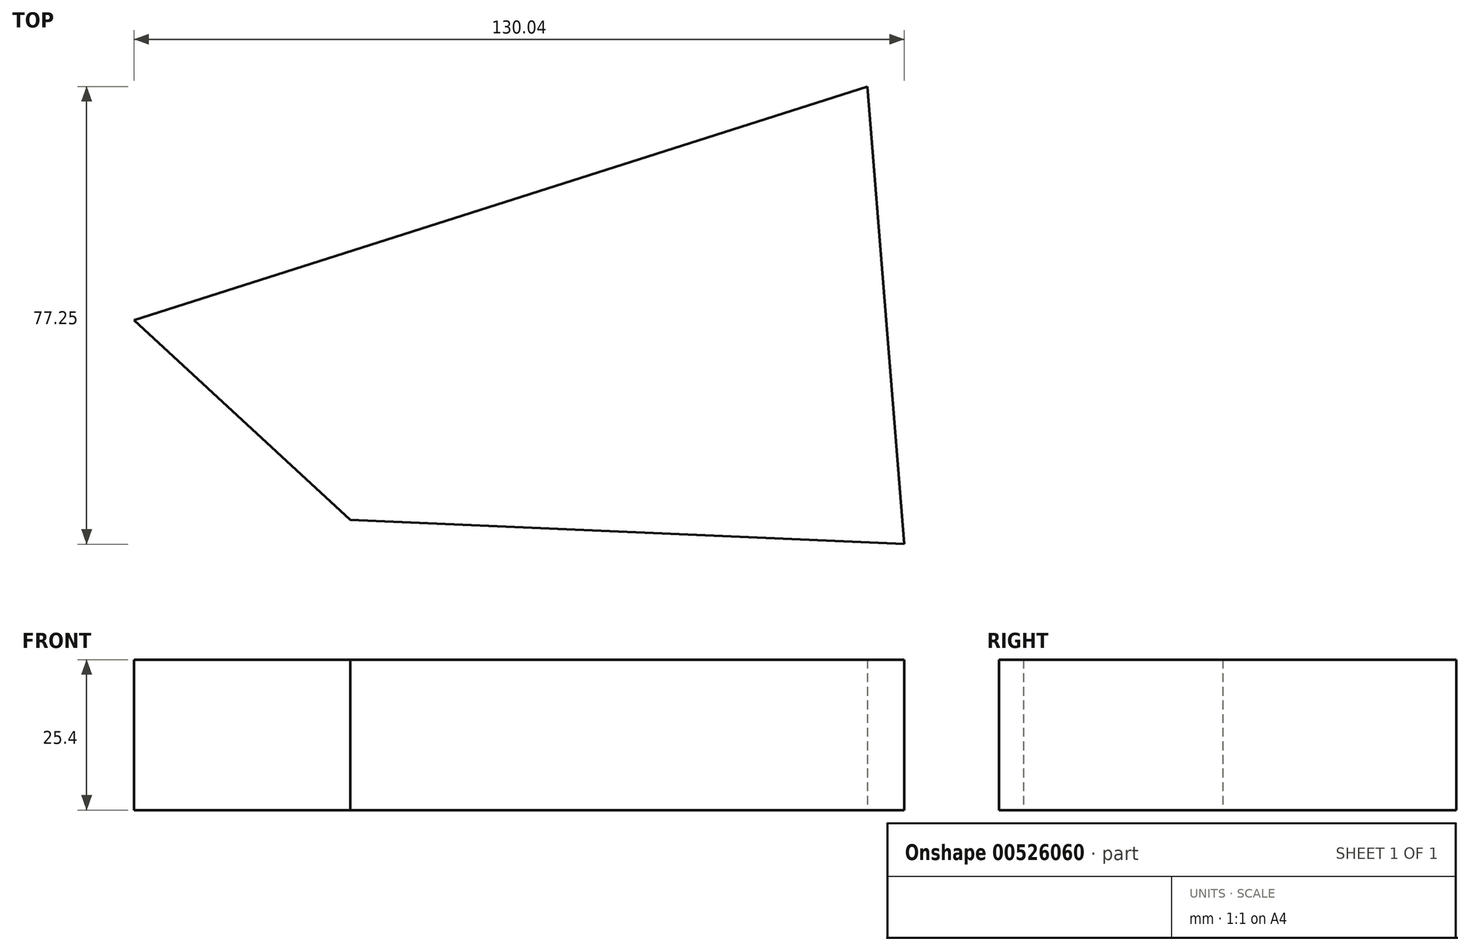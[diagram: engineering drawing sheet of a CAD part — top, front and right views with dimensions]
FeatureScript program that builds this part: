
annotation { "Feature Type Name" : "Feature", "Feature Type Description" : "" }
export const myFeature = defineFeature(function(context is Context, id is Id, definition is map)
    precondition{}
    {
        {
            var Q0;
            Q0=qCreatedBy(makeId("Top.planeOp"),FACE);
            var sketch = newSketch(context, id + "F0", { "sketchPlane" : qUnion([Q0])});
            skLineSegment(sketch, "E0", {"start": v(-100.9, -22.51) * mm, "end": v(-7.34, -26.62) * mm});
            skLineSegment(sketch, "E1", {"start": v(-7.34, -26.62) * mm, "end": v(-13.54, 50.63) * mm});
            skLineSegment(sketch, "E2", {"start": v(-13.54, 50.63) * mm, "end": v(-137.38, 11.2) * mm});
            skLineSegment(sketch, "E3", {"start": v(-137.38, 11.2) * mm, "end": v(-100.9, -22.51) * mm});
            skSolve(sketch);
        }
        {
            var Q0;
            Q0=makeQuery(id+"F0.imprint","IMPRINT",FACE,{"disambiguationData":[TD([[makeQuery(id+"F0.imprint","IMPRINT",EDGE,{"derivedFrom":sQuery(id+"F0.wireOp",EDGE,"E0")}),1.0]])]});
            extrude(context, id + "F1", {"entities" : qUnion([Q0]), "depth" : 25.4 * mm, "offsetDistance" : 25.4 * mm});
        }
    });
